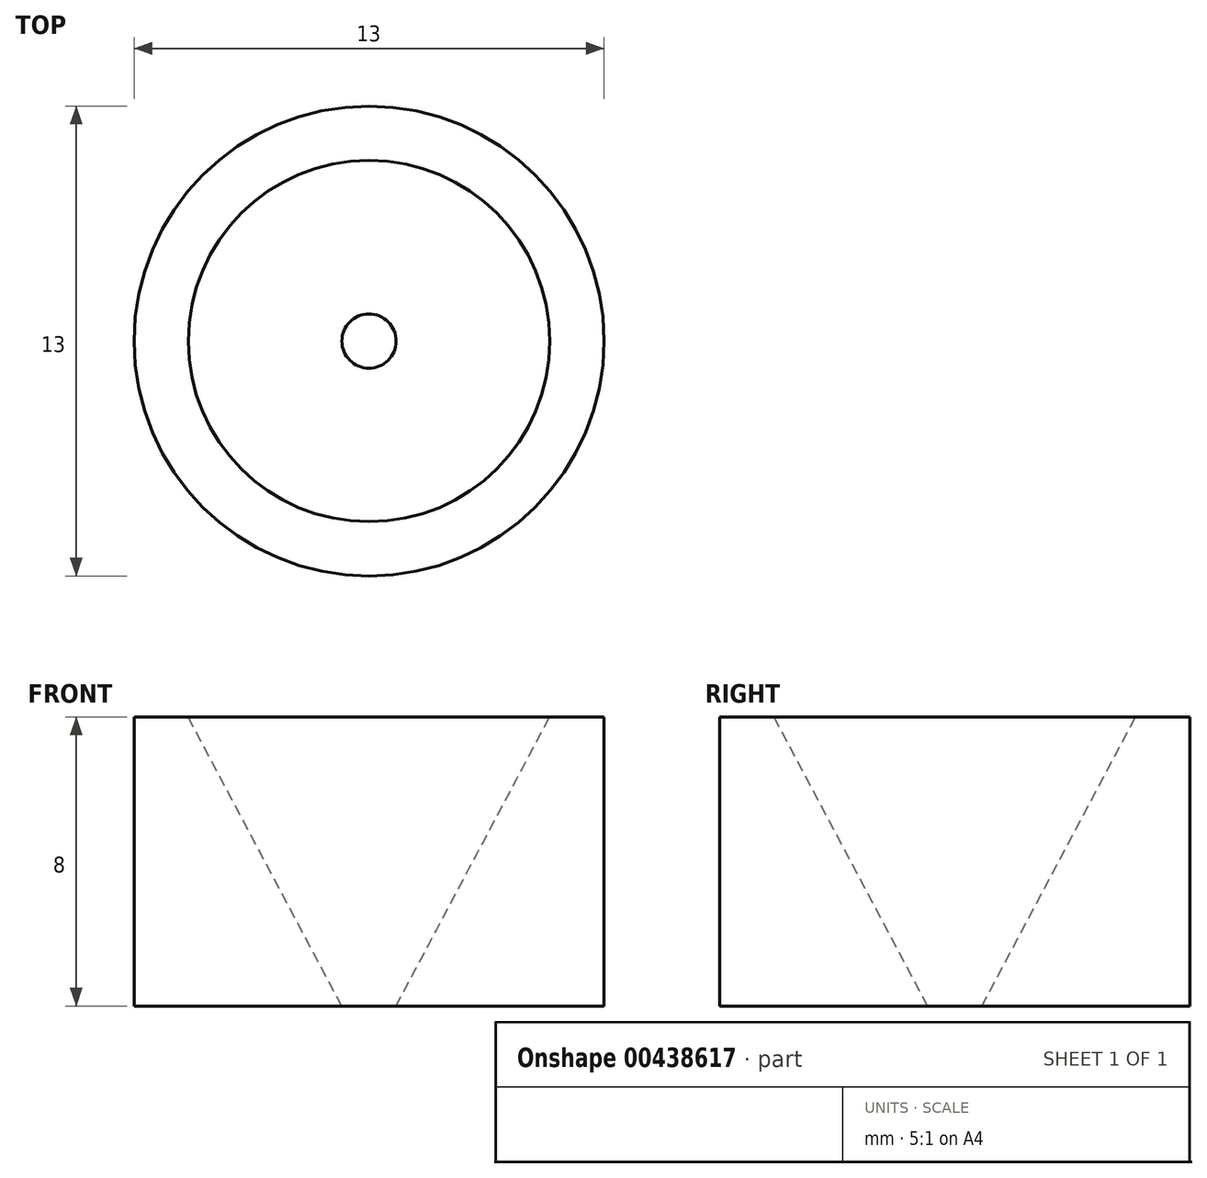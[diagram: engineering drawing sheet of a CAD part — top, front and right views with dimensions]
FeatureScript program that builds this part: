
annotation { "Feature Type Name" : "Feature", "Feature Type Description" : "" }
export const myFeature = defineFeature(function(context is Context, id is Id, definition is map)
    precondition{}
    {
        {
            var Q0;
            Q0=qCreatedBy(makeId("Top.planeOp"),FACE);
            var sketch = newSketch(context, id + "F0", { "sketchPlane" : qUnion([Q0])});
            skCircle(sketch, "E0", {"center": v(0, 0) * mm, "radius": 6.5 * mm});
            skSolve(sketch);
        }
        {
            var Q0;
            Q0 = qSketchRegion(id + "F0", true);
            extrude(context, id + "F1", {"entities" : qUnion([Q0]), "depth" : 8 * mm});
        }
        {
            var Q0;
            Q0=makeQuery(id+"F1.opExtrude","CAP_FACE",FACE,{"disambiguationData":[OSD([sQuery(id+"F0.wireOp",EDGE,"E0")])],"isStart":true});
            var sketch = newSketch(context, id + "F2", { "sketchPlane" : qUnion([Q0])});
            skCircle(sketch, "E1", {"center": v(0, 0) * mm, "radius": 0.75 * mm});
            skSolve(sketch);
        }
        {
            var Q0;
            Q0=makeQuery(id+"F1.opExtrude","CAP_FACE",FACE,{"disambiguationData":[OSD([sQuery(id+"F0.wireOp",EDGE,"E0")])],"isStart":false});
            var sketch = newSketch(context, id + "F3", { "sketchPlane" : qUnion([Q0])});
            skCircle(sketch, "E2", {"center": v(0, 0) * mm, "radius": 5 * mm});
            skSolve(sketch);
        }
        {
            var Q1;
            Q1=makeQuery(id+"F2.imprint","IMPRINT",FACE,{"disambiguationData":[TD([[makeQuery(id+"F2.imprint","IMPRINT",EDGE,{"derivedFrom":sQuery(id+"F2.wireOp",EDGE,"E1")}),1.0]])]});
            var Q2;
            Q2=makeQuery(id+"F3.imprint","IMPRINT",FACE,{"disambiguationData":[TD([[makeQuery(id+"F3.imprint","IMPRINT",EDGE,{"derivedFrom":sQuery(id+"F3.wireOp",EDGE,"E2")}),1.0]])]});
            loft(context, id + "F4", {"operationType" : NewBodyOperationType.REMOVE, "sheetProfilesArray" : [{ "sheetProfileEntities" : qUnion([Q1]) }, { "sheetProfileEntities" : qUnion([Q2]) }]});
        }
    });
